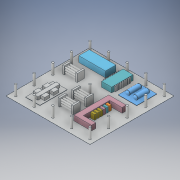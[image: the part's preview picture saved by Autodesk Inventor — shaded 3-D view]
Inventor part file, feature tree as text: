
AUTODESK INVENTOR PART (.ipt)
format: ipt  version: 2016 (Build 200138000, 138)  size: 445,952 bytes
history: native  units: in
note: dims shown in document units (in); Inventor stores cm internally (conversion verified against a paired STEP export)
features: other x3, extrude x1, sketch x1
ambient origin geometry x8: Origin, YZ Plane, XZ Plane, XY Plane, X Axis, Y Axis, Z Axis, Center Point
bodies: Solid1 (feature_tree), Solid2 (feature_tree), Solid3 (feature_tree)
feature tree (5):
  extrude  "Extrusion1"  [1 undecoded]
  sketch  "Sketch1"  dims[d0=0.0in d1=0.0in]
  other  "Sólido3"
  other  "Sólido3:1"
  other  "Sólido3:2"
note: 1 required parameter value undecoded (feature->parameter linkage not recoverable at this tier; creation-order binding heuristic only, values carry confidence <= 0.55)
